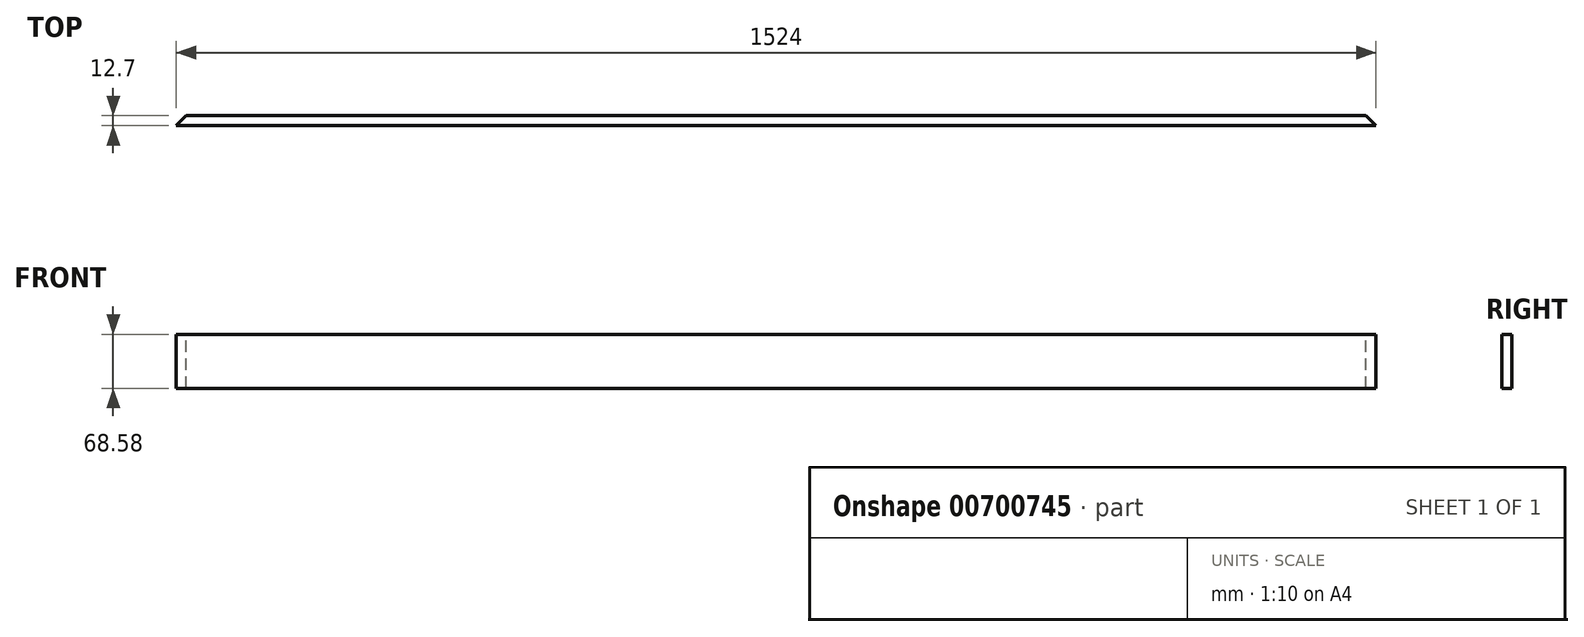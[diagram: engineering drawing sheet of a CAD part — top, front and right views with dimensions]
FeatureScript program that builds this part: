
annotation { "Feature Type Name" : "Feature", "Feature Type Description" : "" }
export const myFeature = defineFeature(function(context is Context, id is Id, definition is map)
    precondition{}
    {
        {
            var Q0;
            Q0=qCreatedBy(makeId("Front.planeOp"),FACE);
            var sketch = newSketch(context, id + "F0", { "sketchPlane" : qUnion([Q0])});
            skLineSegment(sketch, "E0.bottom", {"start": v(0, 0) * mm, "end": v(1524, 0) * mm});
            skLineSegment(sketch, "E0.top", {"start": v(0, 68.58) * mm, "end": v(1524, 68.58) * mm});
            skLineSegment(sketch, "E0.left", {"start": v(0, 0) * mm, "end": v(0, 68.58) * mm});
            skLineSegment(sketch, "E0.right", {"start": v(1524, 0) * mm, "end": v(1524, 68.58) * mm});
            skSolve(sketch);
        }
        {
            var Q0;
            Q0 = qSketchRegion(id + "F0", true);
            extrude(context, id + "F1", {"entities" : qUnion([Q0]), "depth" : 12.7 * mm, "offsetDistance" : 25.4 * mm});
        }
        {
            var Q0;
            Q0=makeQuery(id+"F1.opExtrude","SWEPT_FACE",FACE,{"disambiguationData":[OSD([sQuery(id+"F0.wireOp",EDGE,"E0.top")])]});
            var sketch = newSketch(context, id + "F2", { "sketchPlane" : qUnion([Q0])});
            skLineSegment(sketch, "E1", {"start": v(0, -12.7) * mm, "end": v(0, 0) * mm});
            skLineSegment(sketch, "E2", {"start": v(0, 0) * mm, "end": v(12.7, 0) * mm});
            skLineSegment(sketch, "E3", {"start": v(12.7, 0) * mm, "end": v(0, -12.7) * mm});
            skLineSegment(sketch, "E4", {"start": v(1524, -12.7) * mm, "end": v(1511.3, 0) * mm});
            skLineSegment(sketch, "E5", {"start": v(1511.3, 0) * mm, "end": v(1524, 0) * mm});
            skLineSegment(sketch, "E6", {"start": v(1524, 0) * mm, "end": v(1524, -12.7) * mm});
            skSolve(sketch);
        }
        {
            var Q0;
            Q0 = qSketchRegion(id + "F2", true);
            extrude(context, id + "F3", {"entities" : qUnion([Q0]), "operationType" : NewBodyOperationType.REMOVE, "endBound" : BoundingType.THROUGH_ALL, "oppositeDirection" : true, "depth" : 25.4 * mm, "offsetDistance" : 25.4 * mm});
        }
    });
